# Revit family: Sanitary_Showers_hansgrohe_26620400-Raindance-Select-E-Shower-set-1_
name_source: partatom
category: Plumbing Fixtures
revit_build: Autodesk Revit 2015 (Build: 20140903_1530(x64)
units: mm (PartAtom-declared; Revit-internal decimal feet)

## types (1)
- white/chrome
    BIMobject category = Showers
    BIMobject category code = sanitary-showers
    BIMobject main category = Sanitary
    BIMobject main category code = sanitary
    Brand url = http://www.hansgrohe-int.com
    Default Elevation = 1219.2 mm  [stored 4 ft]
    Design country = Germany
    Edition number = 1
    GTIN code = https://4011097706078
    IFC Classification = Sanitary Terminal
    Manufacturer country = Germany
    Manufacturer name = hansgrohe
    Material main = Chrome
    Product Guid = 1c27f4cf-6dd1-4431-ad1d-39f892c81c74
    Product SKU = 26620400
    Product data url = https://bimobject.com
    Product family = Raindance Select E
    Product group = Wallbar sets
    Product name = 26620400 Raindance Select E Shower set 120 3jet with shower bar 65 cm and soap dish
    QR code = http://bimobject.com

note: [stored X ft] marks values corroborated as IEEE doubles in the binary element streams (Revit-internal decimal feet)

## geometry (parser evidence)
native form markers: Sweep x3
no freeform markers — native parametric forms only
